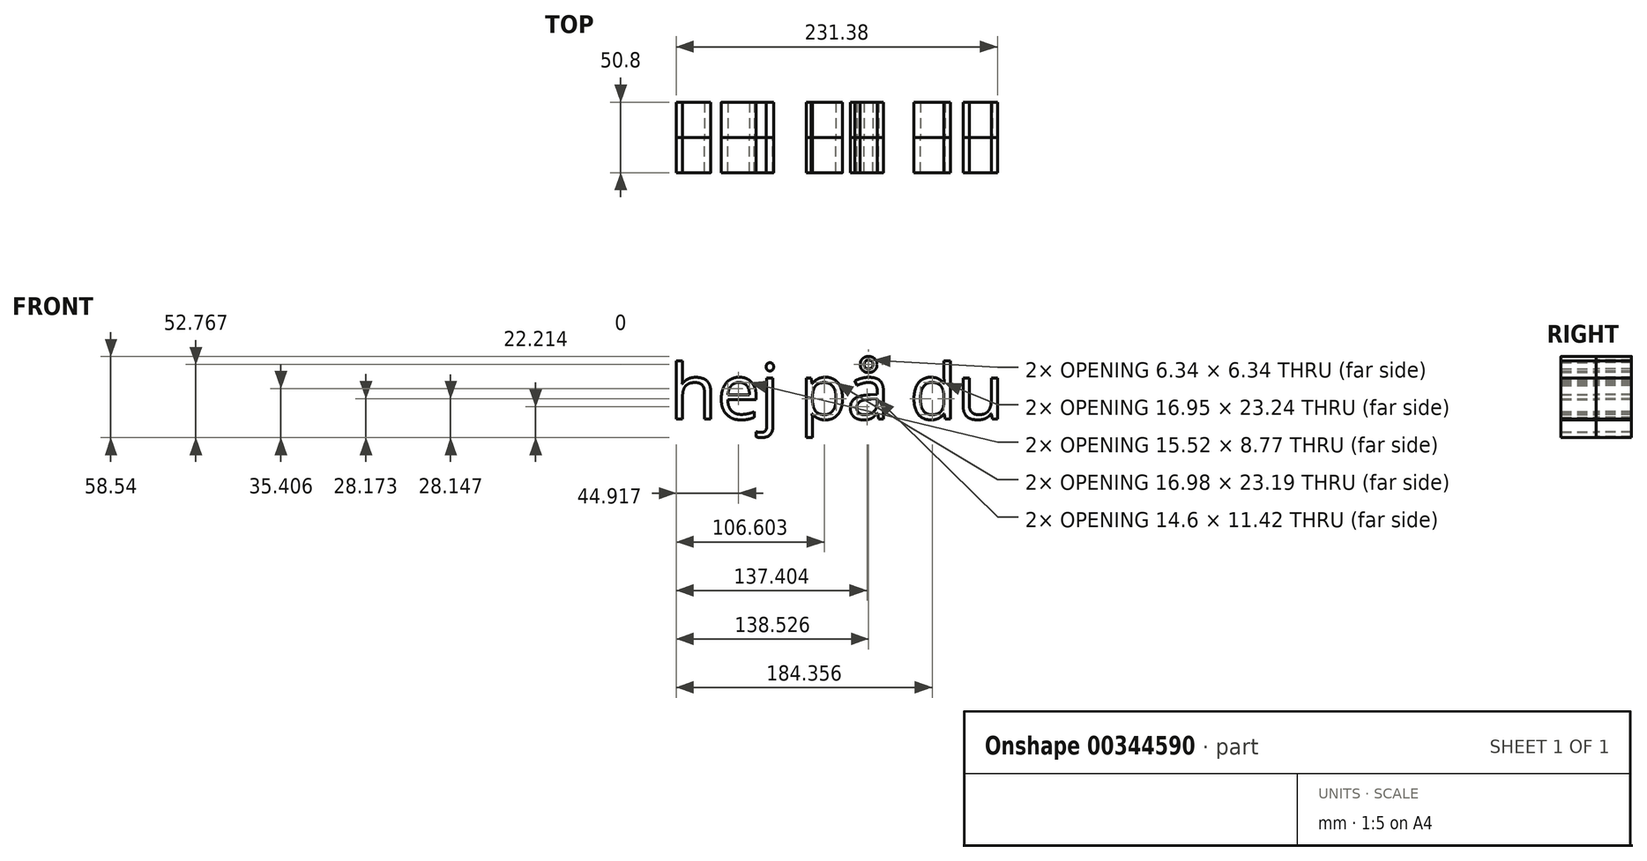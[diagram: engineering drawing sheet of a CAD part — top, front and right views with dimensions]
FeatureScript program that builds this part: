
annotation { "Feature Type Name" : "Feature", "Feature Type Description" : "" }
export const myFeature = defineFeature(function(context is Context, id is Id, definition is map)
    precondition{}
    {
        {
            var Q0;
            Q0=qCreatedBy(makeId("Front.planeOp"),FACE);
            var sketch = newSketch(context, id + "F0", { "sketchPlane" : qUnion([Q0])});
            skText(sketch, "E0", { "text": "hej på du", "fontName": "OpenSans-Regular.ttf"});
            const initialGuessF0  = {"E0": [-0.10383, 0.00826, 1, 0, 0.03994]};
            skSetInitialGuess(sketch, initialGuessF0);
            skSolve(sketch);
        }
        {
            var Q0;
            Q0 = qSketchRegion(id + "F0", true);
            extrude(context, id + "F1", {"entities" : qUnion([Q0]), "depth" : 25.4 * mm});
        }
        {
            var Q0;
            Q0=makeQuery(id+"F1.opExtrude","SWEPT_BODY",BODY,{"disambiguationData":[OSD([sQuery(id+"F0.wireOp",EDGE,"E0.sketch_text.stroke-54"),sQuery(id+"F0.wireOp",EDGE,"E0.sketch_text.stroke-55"),sQuery(id+"F0.wireOp",EDGE,"E0.sketch_text.stroke-56"),sQuery(id+"F0.wireOp",EDGE,"E0.sketch_text.stroke-57"),sQuery(id+"F0.wireOp",EDGE,"E0.sketch_text.stroke-58"),sQuery(id+"F0.wireOp",EDGE,"E0.sketch_text.stroke-59"),sQuery(id+"F0.wireOp",EDGE,"E0.sketch_text.stroke-60"),sQuery(id+"F0.wireOp",EDGE,"E0.sketch_text.stroke-61"),sQuery(id+"F0.wireOp",EDGE,"E0.sketch_text.stroke-62"),sQuery(id+"F0.wireOp",EDGE,"E0.sketch_text.stroke-63"),sQuery(id+"F0.wireOp",EDGE,"E0.sketch_text.stroke-64"),sQuery(id+"F0.wireOp",EDGE,"E0.sketch_text.stroke-65"),sQuery(id+"F0.wireOp",EDGE,"E0.sketch_text.stroke-66"),sQuery(id+"F0.wireOp",EDGE,"E0.sketch_text.stroke-67"),sQuery(id+"F0.wireOp",EDGE,"E0.sketch_text.stroke-68"),sQuery(id+"F0.wireOp",EDGE,"E0.sketch_text.stroke-69"),sQuery(id+"F0.wireOp",EDGE,"E0.sketch_text.stroke-70"),sQuery(id+"F0.wireOp",EDGE,"E0.sketch_text.stroke-71"),sQuery(id+"F0.wireOp",EDGE,"E0.sketch_text.stroke-72"),sQuery(id+"F0.wireOp",EDGE,"E0.sketch_text.stroke-73"),sQuery(id+"F0.wireOp",EDGE,"E0.sketch_text.stroke-74"),sQuery(id+"F0.wireOp",EDGE,"E0.sketch_text.stroke-75"),sQuery(id+"F0.wireOp",EDGE,"E0.sketch_text.stroke-76"),sQuery(id+"F0.wireOp",EDGE,"E0.sketch_text.stroke-77"),sQuery(id+"F0.wireOp",EDGE,"E0.sketch_text.stroke-78")])]});
            var Q1;
            Q1=makeQuery(id+"F1.opExtrude","SWEPT_BODY",BODY,{"disambiguationData":[OSD([sQuery(id+"F0.wireOp",EDGE,"E0.sketch_text.stroke-18"),sQuery(id+"F0.wireOp",EDGE,"E0.sketch_text.stroke-19"),sQuery(id+"F0.wireOp",EDGE,"E0.sketch_text.stroke-20"),sQuery(id+"F0.wireOp",EDGE,"E0.sketch_text.stroke-21"),sQuery(id+"F0.wireOp",EDGE,"E0.sketch_text.stroke-22"),sQuery(id+"F0.wireOp",EDGE,"E0.sketch_text.stroke-23"),sQuery(id+"F0.wireOp",EDGE,"E0.sketch_text.stroke-24"),sQuery(id+"F0.wireOp",EDGE,"E0.sketch_text.stroke-25"),sQuery(id+"F0.wireOp",EDGE,"E0.sketch_text.stroke-26"),sQuery(id+"F0.wireOp",EDGE,"E0.sketch_text.stroke-27"),sQuery(id+"F0.wireOp",EDGE,"E0.sketch_text.stroke-28"),sQuery(id+"F0.wireOp",EDGE,"E0.sketch_text.stroke-29"),sQuery(id+"F0.wireOp",EDGE,"E0.sketch_text.stroke-30"),sQuery(id+"F0.wireOp",EDGE,"E0.sketch_text.stroke-31"),sQuery(id+"F0.wireOp",EDGE,"E0.sketch_text.stroke-32"),sQuery(id+"F0.wireOp",EDGE,"E0.sketch_text.stroke-33"),sQuery(id+"F0.wireOp",EDGE,"E0.sketch_text.stroke-34"),sQuery(id+"F0.wireOp",EDGE,"E0.sketch_text.stroke-35"),sQuery(id+"F0.wireOp",EDGE,"E0.sketch_text.stroke-36")])]});
            var Q2;
            Q2=makeQuery(id+"F1.opExtrude","SWEPT_BODY",BODY,{"disambiguationData":[OSD([sQuery(id+"F0.wireOp",EDGE,"E0.sketch_text.stroke-37"),sQuery(id+"F0.wireOp",EDGE,"E0.sketch_text.stroke-38"),sQuery(id+"F0.wireOp",EDGE,"E0.sketch_text.stroke-39"),sQuery(id+"F0.wireOp",EDGE,"E0.sketch_text.stroke-40"),sQuery(id+"F0.wireOp",EDGE,"E0.sketch_text.stroke-41"),sQuery(id+"F0.wireOp",EDGE,"E0.sketch_text.stroke-42"),sQuery(id+"F0.wireOp",EDGE,"E0.sketch_text.stroke-43"),sQuery(id+"F0.wireOp",EDGE,"E0.sketch_text.stroke-44"),sQuery(id+"F0.wireOp",EDGE,"E0.sketch_text.stroke-45")])]});
            var Q3;
            Q3=makeQuery(id+"F1.opExtrude","SWEPT_BODY",BODY,{"disambiguationData":[OSD([sQuery(id+"F0.wireOp",EDGE,"E0.sketch_text.stroke-0"),sQuery(id+"F0.wireOp",EDGE,"E0.sketch_text.stroke-1"),sQuery(id+"F0.wireOp",EDGE,"E0.sketch_text.stroke-2"),sQuery(id+"F0.wireOp",EDGE,"E0.sketch_text.stroke-3"),sQuery(id+"F0.wireOp",EDGE,"E0.sketch_text.stroke-4"),sQuery(id+"F0.wireOp",EDGE,"E0.sketch_text.stroke-5"),sQuery(id+"F0.wireOp",EDGE,"E0.sketch_text.stroke-6"),sQuery(id+"F0.wireOp",EDGE,"E0.sketch_text.stroke-7"),sQuery(id+"F0.wireOp",EDGE,"E0.sketch_text.stroke-8"),sQuery(id+"F0.wireOp",EDGE,"E0.sketch_text.stroke-9"),sQuery(id+"F0.wireOp",EDGE,"E0.sketch_text.stroke-10"),sQuery(id+"F0.wireOp",EDGE,"E0.sketch_text.stroke-11"),sQuery(id+"F0.wireOp",EDGE,"E0.sketch_text.stroke-12"),sQuery(id+"F0.wireOp",EDGE,"E0.sketch_text.stroke-13"),sQuery(id+"F0.wireOp",EDGE,"E0.sketch_text.stroke-14"),sQuery(id+"F0.wireOp",EDGE,"E0.sketch_text.stroke-15"),sQuery(id+"F0.wireOp",EDGE,"E0.sketch_text.stroke-16"),sQuery(id+"F0.wireOp",EDGE,"E0.sketch_text.stroke-17")])]});
            var Q4;
            Q4=makeQuery(id+"F1.opExtrude","SWEPT_BODY",BODY,{"disambiguationData":[OSD([sQuery(id+"F0.wireOp",EDGE,"E0.sketch_text.stroke-46"),sQuery(id+"F0.wireOp",EDGE,"E0.sketch_text.stroke-47"),sQuery(id+"F0.wireOp",EDGE,"E0.sketch_text.stroke-48"),sQuery(id+"F0.wireOp",EDGE,"E0.sketch_text.stroke-49"),sQuery(id+"F0.wireOp",EDGE,"E0.sketch_text.stroke-50"),sQuery(id+"F0.wireOp",EDGE,"E0.sketch_text.stroke-51"),sQuery(id+"F0.wireOp",EDGE,"E0.sketch_text.stroke-52"),sQuery(id+"F0.wireOp",EDGE,"E0.sketch_text.stroke-53")])]});
            var Q5;
            Q5=makeQuery(id+"F1.opExtrude","SWEPT_BODY",BODY,{"disambiguationData":[OSD([sQuery(id+"F0.wireOp",EDGE,"E0.sketch_text.stroke-106"),sQuery(id+"F0.wireOp",EDGE,"E0.sketch_text.stroke-107"),sQuery(id+"F0.wireOp",EDGE,"E0.sketch_text.stroke-108"),sQuery(id+"F0.wireOp",EDGE,"E0.sketch_text.stroke-109"),sQuery(id+"F0.wireOp",EDGE,"E0.sketch_text.stroke-110"),sQuery(id+"F0.wireOp",EDGE,"E0.sketch_text.stroke-111"),sQuery(id+"F0.wireOp",EDGE,"E0.sketch_text.stroke-112"),sQuery(id+"F0.wireOp",EDGE,"E0.sketch_text.stroke-113"),sQuery(id+"F0.wireOp",EDGE,"E0.sketch_text.stroke-114"),sQuery(id+"F0.wireOp",EDGE,"E0.sketch_text.stroke-115"),sQuery(id+"F0.wireOp",EDGE,"E0.sketch_text.stroke-116"),sQuery(id+"F0.wireOp",EDGE,"E0.sketch_text.stroke-117"),sQuery(id+"F0.wireOp",EDGE,"E0.sketch_text.stroke-118"),sQuery(id+"F0.wireOp",EDGE,"E0.sketch_text.stroke-119"),sQuery(id+"F0.wireOp",EDGE,"E0.sketch_text.stroke-120"),sQuery(id+"F0.wireOp",EDGE,"E0.sketch_text.stroke-121")])]});
            var Q6;
            Q6=makeQuery(id+"F1.opExtrude","SWEPT_BODY",BODY,{"disambiguationData":[OSD([sQuery(id+"F0.wireOp",EDGE,"E0.sketch_text.stroke-79"),sQuery(id+"F0.wireOp",EDGE,"E0.sketch_text.stroke-80"),sQuery(id+"F0.wireOp",EDGE,"E0.sketch_text.stroke-81"),sQuery(id+"F0.wireOp",EDGE,"E0.sketch_text.stroke-82"),sQuery(id+"F0.wireOp",EDGE,"E0.sketch_text.stroke-83"),sQuery(id+"F0.wireOp",EDGE,"E0.sketch_text.stroke-84"),sQuery(id+"F0.wireOp",EDGE,"E0.sketch_text.stroke-85"),sQuery(id+"F0.wireOp",EDGE,"E0.sketch_text.stroke-86"),sQuery(id+"F0.wireOp",EDGE,"E0.sketch_text.stroke-87"),sQuery(id+"F0.wireOp",EDGE,"E0.sketch_text.stroke-88"),sQuery(id+"F0.wireOp",EDGE,"E0.sketch_text.stroke-89"),sQuery(id+"F0.wireOp",EDGE,"E0.sketch_text.stroke-90"),sQuery(id+"F0.wireOp",EDGE,"E0.sketch_text.stroke-91"),sQuery(id+"F0.wireOp",EDGE,"E0.sketch_text.stroke-92"),sQuery(id+"F0.wireOp",EDGE,"E0.sketch_text.stroke-93"),sQuery(id+"F0.wireOp",EDGE,"E0.sketch_text.stroke-94"),sQuery(id+"F0.wireOp",EDGE,"E0.sketch_text.stroke-95"),sQuery(id+"F0.wireOp",EDGE,"E0.sketch_text.stroke-96"),sQuery(id+"F0.wireOp",EDGE,"E0.sketch_text.stroke-97"),sQuery(id+"F0.wireOp",EDGE,"E0.sketch_text.stroke-98"),sQuery(id+"F0.wireOp",EDGE,"E0.sketch_text.stroke-99"),sQuery(id+"F0.wireOp",EDGE,"E0.sketch_text.stroke-100"),sQuery(id+"F0.wireOp",EDGE,"E0.sketch_text.stroke-101"),sQuery(id+"F0.wireOp",EDGE,"E0.sketch_text.stroke-102"),sQuery(id+"F0.wireOp",EDGE,"E0.sketch_text.stroke-103"),sQuery(id+"F0.wireOp",EDGE,"E0.sketch_text.stroke-104"),sQuery(id+"F0.wireOp",EDGE,"E0.sketch_text.stroke-105")])]});
            var Q7;
            Q7=makeQuery(id+"F1.opExtrude","SWEPT_BODY",BODY,{"disambiguationData":[OSD([sQuery(id+"F0.wireOp",EDGE,"E0.sketch_text.stroke-122"),sQuery(id+"F0.wireOp",EDGE,"E0.sketch_text.stroke-123"),sQuery(id+"F0.wireOp",EDGE,"E0.sketch_text.stroke-124"),sQuery(id+"F0.wireOp",EDGE,"E0.sketch_text.stroke-125"),sQuery(id+"F0.wireOp",EDGE,"E0.sketch_text.stroke-126"),sQuery(id+"F0.wireOp",EDGE,"E0.sketch_text.stroke-127"),sQuery(id+"F0.wireOp",EDGE,"E0.sketch_text.stroke-128"),sQuery(id+"F0.wireOp",EDGE,"E0.sketch_text.stroke-129"),sQuery(id+"F0.wireOp",EDGE,"E0.sketch_text.stroke-130"),sQuery(id+"F0.wireOp",EDGE,"E0.sketch_text.stroke-131"),sQuery(id+"F0.wireOp",EDGE,"E0.sketch_text.stroke-132"),sQuery(id+"F0.wireOp",EDGE,"E0.sketch_text.stroke-133"),sQuery(id+"F0.wireOp",EDGE,"E0.sketch_text.stroke-134"),sQuery(id+"F0.wireOp",EDGE,"E0.sketch_text.stroke-135"),sQuery(id+"F0.wireOp",EDGE,"E0.sketch_text.stroke-136"),sQuery(id+"F0.wireOp",EDGE,"E0.sketch_text.stroke-137"),sQuery(id+"F0.wireOp",EDGE,"E0.sketch_text.stroke-138"),sQuery(id+"F0.wireOp",EDGE,"E0.sketch_text.stroke-139"),sQuery(id+"F0.wireOp",EDGE,"E0.sketch_text.stroke-140"),sQuery(id+"F0.wireOp",EDGE,"E0.sketch_text.stroke-141"),sQuery(id+"F0.wireOp",EDGE,"E0.sketch_text.stroke-142"),sQuery(id+"F0.wireOp",EDGE,"E0.sketch_text.stroke-143"),sQuery(id+"F0.wireOp",EDGE,"E0.sketch_text.stroke-144"),sQuery(id+"F0.wireOp",EDGE,"E0.sketch_text.stroke-145")])]});
            var Q8;
            Q8=makeQuery(id+"F1.opExtrude","SWEPT_BODY",BODY,{"disambiguationData":[OSD([sQuery(id+"F0.wireOp",EDGE,"E0.sketch_text.stroke-146"),sQuery(id+"F0.wireOp",EDGE,"E0.sketch_text.stroke-147"),sQuery(id+"F0.wireOp",EDGE,"E0.sketch_text.stroke-148"),sQuery(id+"F0.wireOp",EDGE,"E0.sketch_text.stroke-149"),sQuery(id+"F0.wireOp",EDGE,"E0.sketch_text.stroke-150"),sQuery(id+"F0.wireOp",EDGE,"E0.sketch_text.stroke-151"),sQuery(id+"F0.wireOp",EDGE,"E0.sketch_text.stroke-152"),sQuery(id+"F0.wireOp",EDGE,"E0.sketch_text.stroke-153"),sQuery(id+"F0.wireOp",EDGE,"E0.sketch_text.stroke-154"),sQuery(id+"F0.wireOp",EDGE,"E0.sketch_text.stroke-155"),sQuery(id+"F0.wireOp",EDGE,"E0.sketch_text.stroke-156"),sQuery(id+"F0.wireOp",EDGE,"E0.sketch_text.stroke-157"),sQuery(id+"F0.wireOp",EDGE,"E0.sketch_text.stroke-158"),sQuery(id+"F0.wireOp",EDGE,"E0.sketch_text.stroke-159"),sQuery(id+"F0.wireOp",EDGE,"E0.sketch_text.stroke-160"),sQuery(id+"F0.wireOp",EDGE,"E0.sketch_text.stroke-161"),sQuery(id+"F0.wireOp",EDGE,"E0.sketch_text.stroke-162")])]});
            var Q9;
            Q9=qCreatedBy(makeId("Front.planeOp"),FACE);
            mirror(context, id + "F2", {"entities" : qUnion([Q0, Q1, Q2, Q3, Q4, Q5, Q6, Q7, Q8]), "mirrorPlane" : qUnion([Q9])});
        }
    });
